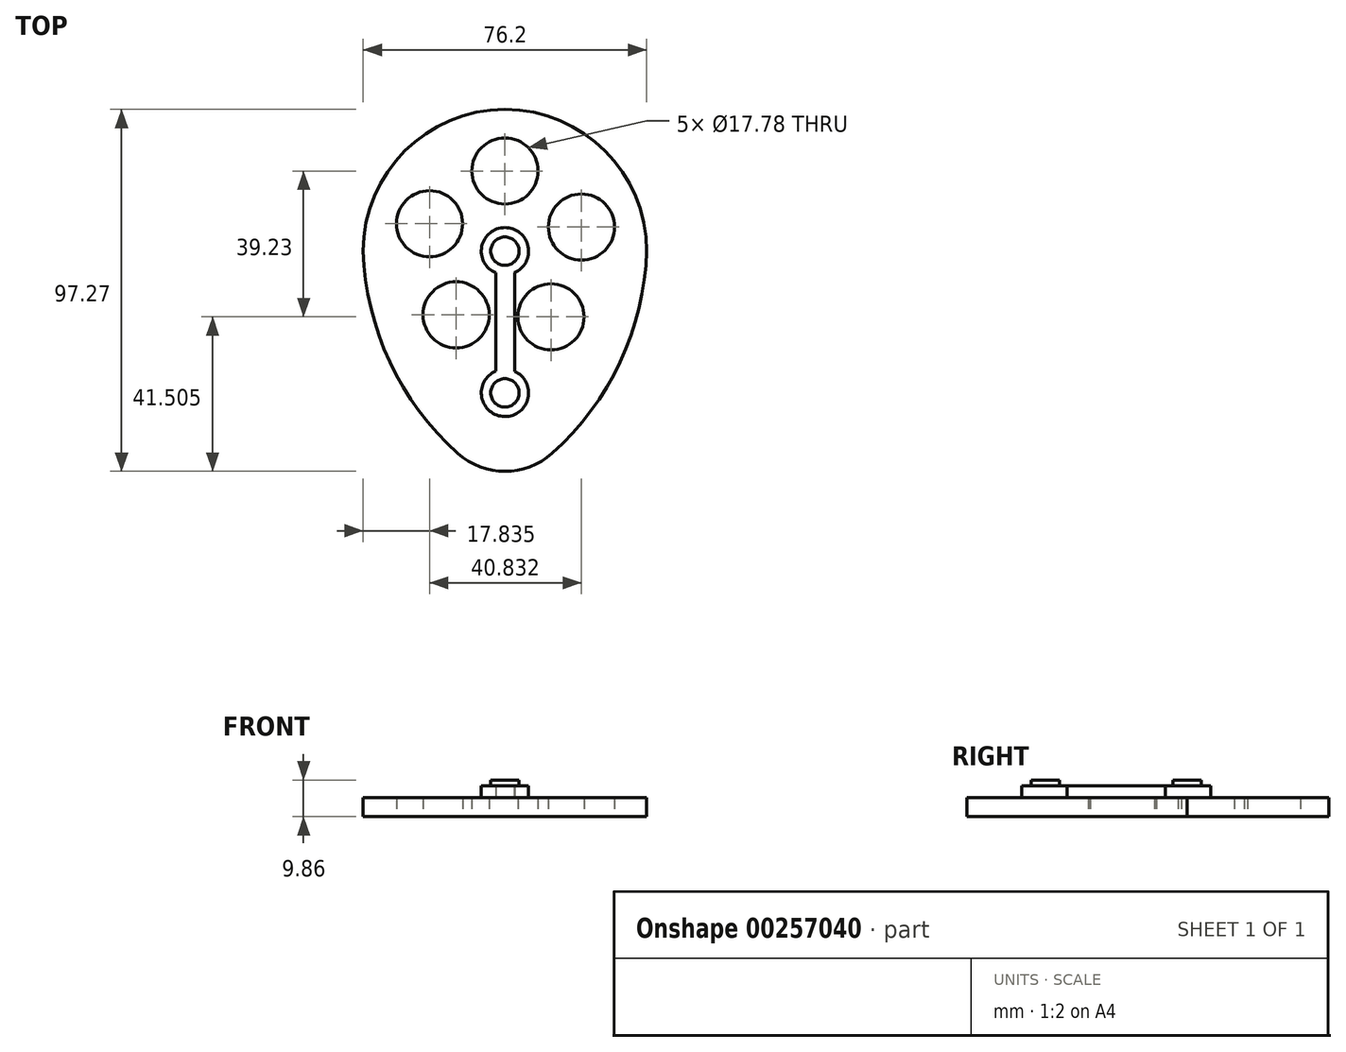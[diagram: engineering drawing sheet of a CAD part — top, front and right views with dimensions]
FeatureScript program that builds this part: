
annotation { "Feature Type Name" : "Feature", "Feature Type Description" : "" }
export const myFeature = defineFeature(function(context is Context, id is Id, definition is map)
    precondition{}
    {
        {
            var Q0;
            Q0=qCreatedBy(makeId("Top.planeOp"),FACE);
            var sketch = newSketch(context, id + "F0", { "sketchPlane" : qUnion([Q0])});
            skArc(sketch, "E0", {"start": v(38.1, 0) * mm, "mid": v(0, 38.1) * mm, "end": v(-38.1, 0) * mm});
            skArc(sketch, "E1", {"start": v(-38.1, 0) * mm, "mid": v(-27.28, -36.69) * mm, "end": v(0, -63.5) * mm});
            skArc(sketch, "E2", {"start": v(0, -63.5) * mm, "mid": v(27.28, -36.69) * mm, "end": v(38.1, 0) * mm});
            skCircle(sketch, "E3", {"center": v(0, 21.57) * mm, "radius": 8.9 * mm});
            skCircle(sketch, "E4.1.0", {"center": v(20.57, 6.48) * mm, "radius": 8.9 * mm});
            skCircle(sketch, "E4.2.0", {"center": v(12.37, -17.67) * mm, "radius": 8.9 * mm});
            skCircle(sketch, "E4.3.0", {"center": v(-13.13, -17.1) * mm, "radius": 8.9 * mm});
            skCircle(sketch, "E4.4.0", {"center": v(-20.26, 7.38) * mm, "radius": 8.9 * mm});
            skLineSegment(sketch, "E4.anchor1", {"start": v(0, 0) * mm, "end": v(0, 21.57) * mm, "construction": true});
            skLineSegment(sketch, "E4.anchor2", {"start": v(0, 0) * mm, "end": v(-20.26, 7.38) * mm, "construction": true});
            skSolve(sketch);
        }
        {
            var Q0;
            Q0 = qSketchRegion(id + "F0", true);
            extrude(context, id + "F1", {"entities" : qUnion([Q0]), "depth" : 5.08 * mm});
        }
        {
            var Q0;
            Q0=makeQuery(id+"F1.opExtrude","CAP_FACE",FACE,{"disambiguationData":[OSD([sQuery(id+"F0.wireOp",EDGE,"E0"),sQuery(id+"F0.wireOp",EDGE,"E1"),sQuery(id+"F0.wireOp",EDGE,"E2"),sQuery(id+"F0.wireOp",EDGE,"E3"),sQuery(id+"F0.wireOp",EDGE,"E4.1.0"),sQuery(id+"F0.wireOp",EDGE,"E4.2.0"),sQuery(id+"F0.wireOp",EDGE,"E4.3.0"),sQuery(id+"F0.wireOp",EDGE,"E4.4.0")])],"isStart":false});
            var sketch = newSketch(context, id + "F2", { "sketchPlane" : qUnion([Q0])});
            skCircle(sketch, "E5", {"center": v(0, 0) * mm, "radius": 6.35 * mm});
            skCircle(sketch, "E6", {"center": v(0, -38.1) * mm, "radius": 6.35 * mm});
            skLineSegment(sketch, "E7", {"start": v(0, -31.75) * mm, "end": v(2.6, -32.3) * mm});
            skLineSegment(sketch, "E8", {"start": v(-2.49, -5.84) * mm, "end": v(-2.49, -32.26) * mm});
            skLineSegment(sketch, "E9", {"start": v(2.6, -5.84) * mm, "end": v(2.6, -32.3) * mm});
            skLineSegment(sketch, "E10", {"start": v(2.49, -5.84) * mm, "end": v(2.6, -5.84) * mm});
            skSolve(sketch);
        }
        {
            var Q0;
            Q0=makeQuery(id+"F1.opExtrude","SWEPT_EDGE",EDGE,{"disambiguationData":[OSD([sQuery(id+"F0.wireOp",EDGE,"E1"),sQuery(id+"F0.wireOp",EDGE,"E2")])]});
            fillet(context, id + "F3", {"entities" : qUnion([Q0]), "radius" : 19.05 * mm, "tangentPropagation" : true, "allowEdgeOverflow" : false});
        }
        {
            var Q0;
            Q0 = qSketchRegion(id + "F2", true);
            extrude(context, id + "F4", {"entities" : qUnion([Q0]), "operationType" : NewBodyOperationType.ADD, "depth" : 3.17 * mm});
        }
        {
            var Q0;
            Q0=makeQuery(id+"F4.opExtrude","CAP_FACE",FACE,{"disambiguationData":[OSD([sQuery(id+"F2.wireOp",EDGE,"E5"),sQuery(id+"F2.wireOp",EDGE,"E6"),sQuery(id+"F2.wireOp",EDGE,"E8"),sQuery(id+"F2.wireOp",EDGE,"E9"),sQuery(id+"F2.wireOp",EDGE,"E10")])],"isStart":false});
            var sketch = newSketch(context, id + "F5", { "sketchPlane" : qUnion([Q0])});
            skCircle(sketch, "E11", {"center": v(0, -38.1) * mm, "radius": 3.81 * mm});
            skCircle(sketch, "E12", {"center": v(0, 0) * mm, "radius": 3.81 * mm});
            skSolve(sketch);
        }
        {
            var Q0;
            Q0 = qSketchRegion(id + "F5", true);
            extrude(context, id + "F6", {"entities" : qUnion([Q0]), "operationType" : NewBodyOperationType.ADD, "depth" : 1.6 * mm});
        }
    });
